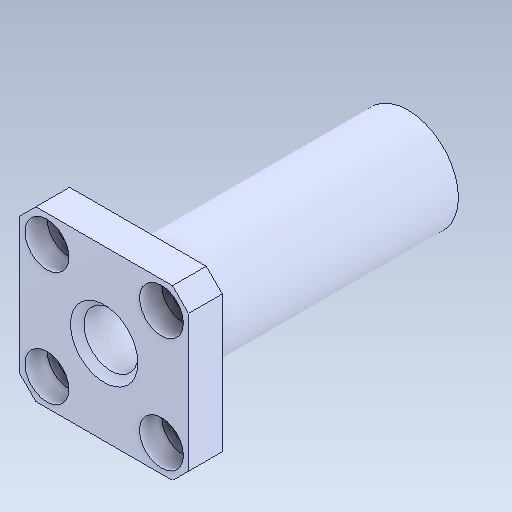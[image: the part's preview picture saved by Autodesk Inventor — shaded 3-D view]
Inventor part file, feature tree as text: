
AUTODESK INVENTOR PART (.ipt)
format: ipt  version: 2020 (Build 240168000, 168)  size: 163,328 bytes
history: native  units: in
note: dims shown in document units (in); Inventor stores cm internally (conversion verified against a paired STEP export)
features: extrude x1, sketch x1, chamfer x1
ambient origin geometry x8: Origin, YZ Plane, XZ Plane, XY Plane, X Axis, Y Axis, Z Axis, Center Point
bodies: Solid1 (feature_tree)
feature tree (3):
  extrude  "Extrusion1"  [1 undecoded]
  sketch  "Sketch1"  dims[d0=1.5748in d1=0.0in]
  chamfer  "Chamfer1"  [1 undecoded]
note: 2 required parameter values undecoded (feature->parameter linkage not recoverable at this tier; creation-order binding heuristic only, values carry confidence <= 0.55)
